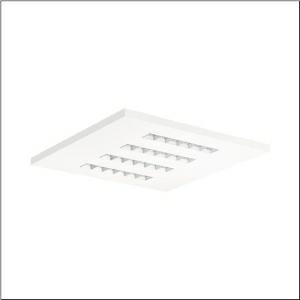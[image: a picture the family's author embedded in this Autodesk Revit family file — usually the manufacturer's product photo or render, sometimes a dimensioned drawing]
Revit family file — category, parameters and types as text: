
# Revit family: silica_r__21_square_51mx6mds44w_aad7
name_source: partatom
category: Lighting Fixtures
units: mm (PartAtom-declared; Revit-internal decimal feet)

## family parameters
Cut with Voids When Loaded = No
Host = Face
Light Source = No
Part Type = Normal
Room Calculation Point = No
Round Connector Dimension = Use Diameter
Shared = No

## types (1)
- --- (1 x LED, 4600 lm, 27.2 W, 4000K)
    Apparent Load = 27 VA
    CIE Flux Codes = 83 98 100 100 100
    Color Rendering = 80
    Color Temperature = 4000K
    Default Elevation = 1800 mm
    Description = Silica® 21 Square, office luminaire, primary light control with lens, of PMMA, primary anti-glare with reflector, of PC, white, CAT 2 (L<= 3000cd/m²), light emission: direct distribution, primary light characteristic: symmetric, installation type: lay-in mounting, LED, rated luminous flux: 4.600lm, luminous efficacy: 169lm/W, light colour: 840, colour temperature: 4000K, control gear: DALI 2, with terminal, 5-pole, mains connection: 220..240V, AC, 50/60Hz, rated input power: 27.2W, luminaire housing, of sheet steel, coated, traffic white (RAL 9016), module: M600, length: 597mm, width: 597mm, height: 33mm, protection rating (complete): IP20, insulation class (complete): insulation class I (protective earthing), certification: CE, ENEC, VDE, permissible operating ambient temperature: -20..+40°C, standard: EN 50419, packaging unit: 1 piece
    Height = 0 mm  [stored 0 ft]
    Lamp = 1 x LED
    Lamp Light Flux = 4600 lm
    Lamp Power = 27.2 W
    Lamp count = 1
    Length = 597 mm
    Luminous efficacy = 169 lm/W
    Manufacturer = Siteco
    ModVariant = No
    Model = 51MX6MDS44W
    Mounting Place = Ceiling
    Mounting Type = Recessed
    Number of Poles = 1
    OnlyDefault = Yes
    Power Factor = 1
    Product Name = Silica® 21 Square
    Product group = office luminaire | ceiling recessed
    ProductGroupID = 401
    Protection Class = Protection class I
    Protection Degree = IP 20
    RLX_Detail_Level = 1
    RLX_Emergency_Light_Flux = 0 lm
    RLX_Emergency_Type = 0
    RLX_Emergency_Type_DB = No
    RlxData = <blob elided: 18645 chars, md5=bb1e944c>
    Socket = socket
    Standby Power = 0 W
    System Light Flux = 4600 lm
    System Power = 27 W
    Type Comments = factory setting: luminous flux: 100 % | dim-lin: 254 | 366 mA
    Type Image = l_1275220.jpg
    URL = http://relux.com
    VarID = @adj_083782
    Voltage = 0 V
    Weight = 0.00 kg
    Width = 597 mm

note: [stored X ft] marks values corroborated as IEEE doubles in the binary element streams (Revit-internal decimal feet)

## geometry (parser evidence)
native form markers: Blend x4, Sweep x11
no freeform markers — native parametric forms only
